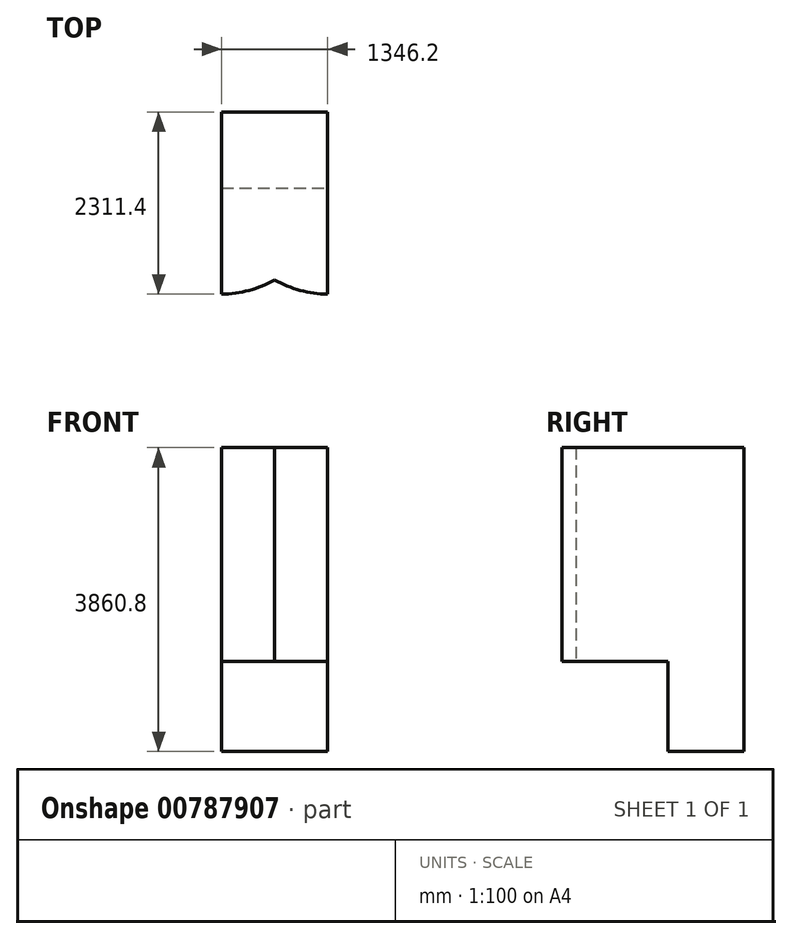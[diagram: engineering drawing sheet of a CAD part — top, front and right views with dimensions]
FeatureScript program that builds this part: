
annotation { "Feature Type Name" : "Feature", "Feature Type Description" : "" }
export const myFeature = defineFeature(function(context is Context, id is Id, definition is map)
    precondition{}
    {
        {
            var Q0;
            Q0=qCreatedBy(makeId("Top.planeOp"),FACE);
            var sketch = newSketch(context, id + "F0", { "sketchPlane" : qUnion([Q0])});
            skLineSegment(sketch, "E0.bottom", {"start": v(0, 0) * mm, "end": v(1346.2, 0) * mm});
            skLineSegment(sketch, "E0.top", {"start": v(0, 965.2) * mm, "end": v(1346.2, 965.2) * mm});
            skLineSegment(sketch, "E0.left", {"start": v(0, 0) * mm, "end": v(0, 965.2) * mm});
            skLineSegment(sketch, "E0.right", {"start": v(1346.2, 0) * mm, "end": v(1346.2, 965.2) * mm});
            skSolve(sketch);
        }
        {
            var Q0;
            Q0=makeQuery(id+"F0.imprint","IMPRINT",FACE,{"disambiguationData":[TD([[makeQuery(id+"F0.imprint","IMPRINT",EDGE,{"derivedFrom":sQuery(id+"F0.wireOp",EDGE,"E0.bottom")}),1.0]])]});
            extrude(context, id + "F1", {"entities" : qUnion([Q0]), "depth" : 3860.8 * mm, "offsetDistance" : 25.4 * mm});
        }
        {
            var Q0;
            Q0=makeQuery(id+"F1.opExtrude","SWEPT_FACE",FACE,{"disambiguationData":[OSD([sQuery(id+"F0.wireOp",EDGE,"E0.bottom")])]});
            var sketch = newSketch(context, id + "F2", { "sketchPlane" : qUnion([Q0])});
            skLineSegment(sketch, "E1", {"start": v(0, 1143) * mm, "end": v(1346.2, 1143) * mm});
            skSolve(sketch);
        }
        {
            var Q0;
            Q0 = qSketchRegion(id + "F2", true);
            var Q1;
            Q1 = qConstructionFilter(qBodyType(qCreatedBy(id + "F2" ,EDGE), BodyType.WIRE), ConstructionObject.NO);
            var Q2;
            Q2=makeQuery(id+"F1.opExtrude","SWEPT_EDGE",EDGE,{"disambiguationData":[OSD([sQuery(id+"F0.wireOp",EDGE,"E0.bottom"),sQuery(id+"F0.wireOp",EDGE,"E0.left")])]});
            revolve(context, id + "F3", {"bodyType" : ToolBodyType.SURFACE, "surfaceOperationType" : NewSurfaceOperationType.NEW, "entities" : qUnion([Q0]), "surfaceEntities" : qUnion([Q1]), "axis" : qUnion([Q2]), "revolveType" : RevolveType.TWO_DIRECTIONS, "angle" : 90 * degree, "angleBack" : 0 * degree});
        }
        {
            var Q0;
            Q0 = qSketchRegion(id + "F2", true);
            var Q1;
            Q1 = qConstructionFilter(qBodyType(qCreatedBy(id + "F2" ,EDGE), BodyType.WIRE), ConstructionObject.NO);
            var Q2;
            {var subQ0=sQuery(id+"F2.wireOp",VERTEX,"E1.end");Q2=makeQuery(id+"F5.boolean.opBoolean","MERGE",EDGE,{"derivedFrom":[makeQuery(id+"F1.opExtrude","SWEPT_EDGE",EDGE,{"disambiguationData":[OSD([sQuery(id+"F0.wireOp",EDGE,"E0.bottom"),sQuery(id+"F0.wireOp",EDGE,"E0.right")])]}),makeQuery(id+"F5.opExtrude","SWEPT_EDGE",EDGE,{"disambiguationData":[OSD([subQ0]),TDD([makeQuery(id+"F3.opRevolve","CAP_VERTEX",VERTEX,{"disambiguationData":[OSD([subQ0])],"isStart":true})])]})]});}
            revolve(context, id + "F4", {"bodyType" : ToolBodyType.SURFACE, "surfaceOperationType" : NewSurfaceOperationType.NEW, "entities" : qUnion([Q0]), "surfaceEntities" : qUnion([Q1]), "axis" : qUnion([Q2]), "revolveType" : RevolveType.TWO_DIRECTIONS, "angle" : 0 * degree, "angleBack" : 270 * degree});
        }
        {
            var Q0;
            Q0=makeQuery(id+"F3.opRevolve","SWEPT_FACE",FACE,{"disambiguationData":[OSD([sQuery(id+"F2.wireOp",EDGE,"E1")])]});
            var Q1;
            Q1=makeQuery(id+"F4.opRevolve","SWEPT_FACE",FACE,{"disambiguationData":[OSD([sQuery(id+"F2.wireOp",EDGE,"E1")])]});
            extrude(context, id + "F5", {"entities" : qUnion([Q0, Q1]), "operationType" : NewBodyOperationType.ADD, "oppositeDirection" : true, "depth" : 2717.8 * mm, "offsetDistance" : 25.4 * mm});
        }
    });
